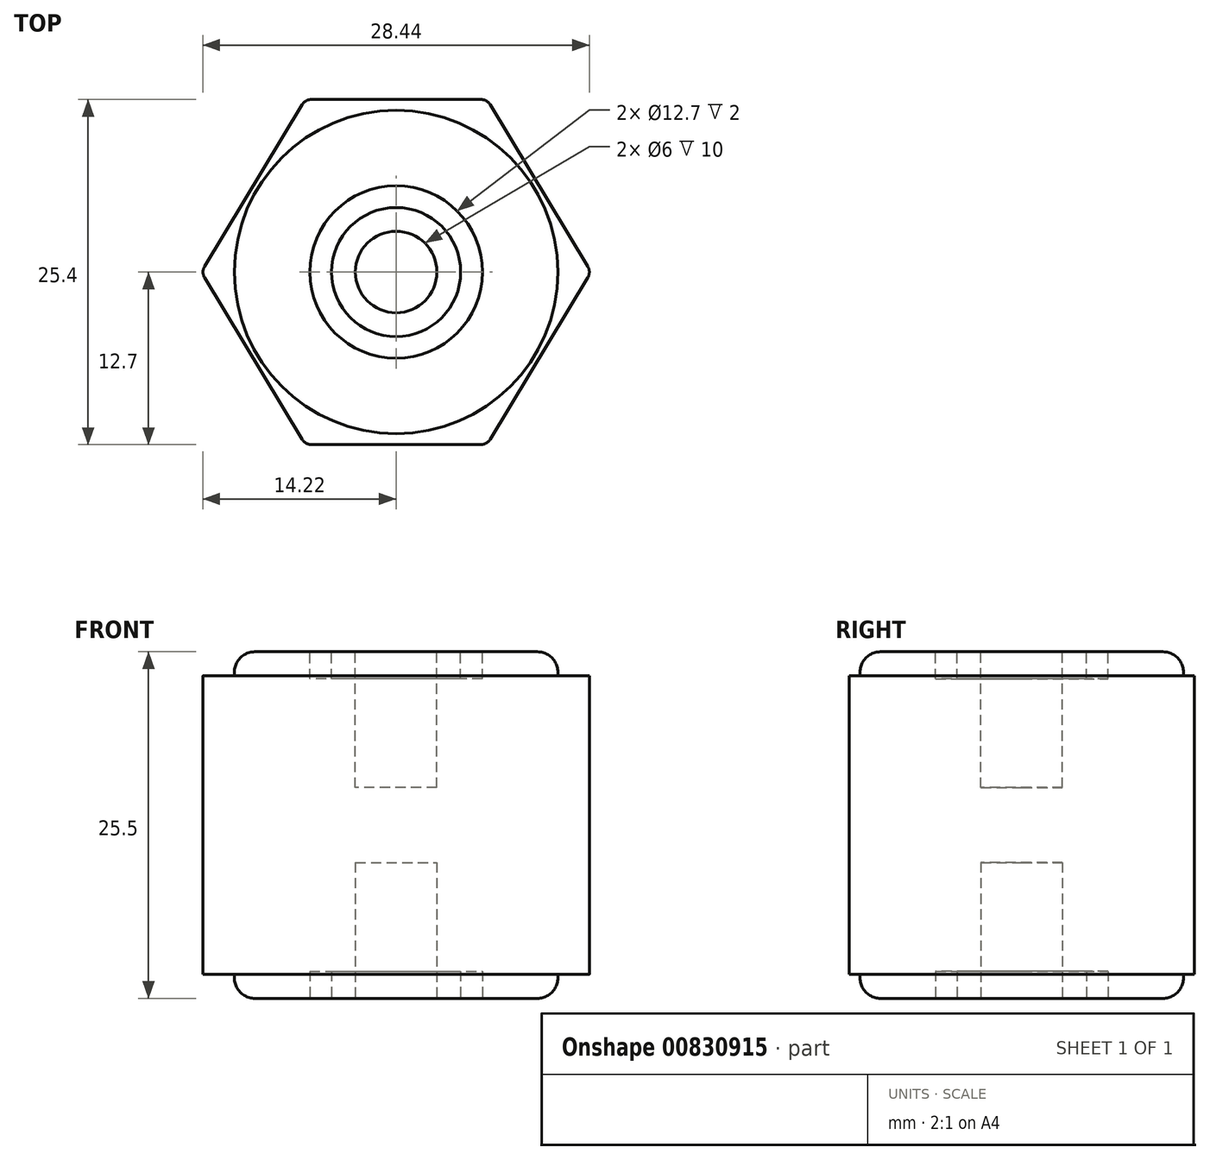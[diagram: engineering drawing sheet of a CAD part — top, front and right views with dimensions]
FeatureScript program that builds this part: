
annotation { "Feature Type Name" : "Feature", "Feature Type Description" : "" }
export const myFeature = defineFeature(function(context is Context, id is Id, definition is map)
    precondition{}
    {
        {
            var Q0;
            Q0=qCreatedBy(makeId("Top.planeOp"),FACE);
            var sketch = newSketch(context, id + "F0", { "sketchPlane" : qUnion([Q0])});
            skCircle(sketch, "E0", {"center": v(0, 0) * mm, "radius": 14.35 * mm});
            skLineSegment(sketch, "E1", {"start": v(-16.5, 12.7) * mm, "end": v(14.66, 12.7) * mm});
            skLineSegment(sketch, "E2", {"start": v(-20.14, -12.7) * mm, "end": v(19.5, -12.7) * mm});
            skLineSegment(sketch, "E3", {"start": v(6.68, 12.7) * mm, "end": v(14.35, 0) * mm});
            skLineSegment(sketch, "E4", {"start": v(14.35, 0) * mm, "end": v(6.68, -12.7) * mm});
            skLineSegment(sketch, "E5", {"start": v(-6.68, 12.7) * mm, "end": v(-14.35, 0) * mm});
            skLineSegment(sketch, "E6", {"start": v(-14.35, 0) * mm, "end": v(-6.68, -12.7) * mm});
            skSolve(sketch);
        }
        {
            var Q0;
            {var subQ1=sQuery(id+"F0.wireOp",EDGE,"E3");Q0=makeQuery(id+"F0.imprint","IMPRINT",FACE,{"disambiguationData":[TD([[makeQuery(id+"F0.imprint","IMPRINT",EDGE,{"derivedFrom":subQ1}),-1.0]])]});}
            extrude(context, id + "F1", {"entities" : qUnion([Q0]), "depth" : 22 * mm, "offsetDistance" : 25 * mm});
        }
        {
            var Q0;
            Q0=makeQuery(id+"F1.opExtrude","CAP_FACE",FACE,{"disambiguationData":[OSD([sQuery(id+"F0.wireOp",EDGE,"E1"),sQuery(id+"F0.wireOp",EDGE,"E2"),sQuery(id+"F0.wireOp",EDGE,"E3"),sQuery(id+"F0.wireOp",EDGE,"E4"),sQuery(id+"F0.wireOp",EDGE,"E5"),sQuery(id+"F0.wireOp",EDGE,"E6")])],"isStart":false});
            var sketch = newSketch(context, id + "F2", { "sketchPlane" : qUnion([Q0])});
            skCircle(sketch, "E7", {"center": v(0, 0) * mm, "radius": 11.9 * mm});
            skSolve(sketch);
        }
        {
            var Q0;
            Q0 = qSketchRegion(id + "F2", true);
            extrude(context, id + "F3", {"entities" : qUnion([Q0]), "operationType" : NewBodyOperationType.ADD, "depth" : 1.75 * mm, "offsetDistance" : 25 * mm});
        }
        {
            var Q0;
            Q0=makeQuery(id+"F1.opExtrude","CAP_FACE",FACE,{"disambiguationData":[OSD([sQuery(id+"F0.wireOp",EDGE,"E1"),sQuery(id+"F0.wireOp",EDGE,"E2"),sQuery(id+"F0.wireOp",EDGE,"E3"),sQuery(id+"F0.wireOp",EDGE,"E4"),sQuery(id+"F0.wireOp",EDGE,"E5"),sQuery(id+"F0.wireOp",EDGE,"E6")])],"isStart":true});
            var sketch = newSketch(context, id + "F4", { "sketchPlane" : qUnion([Q0])});
            skCircle(sketch, "E8", {"center": v(0, 0) * mm, "radius": 11.9 * mm});
            skSolve(sketch);
        }
        {
            var Q0;
            Q0 = qSketchRegion(id + "F4", true);
            extrude(context, id + "F5", {"entities" : qUnion([Q0]), "operationType" : NewBodyOperationType.ADD, "depth" : 1.75 * mm, "offsetDistance" : 25 * mm});
        }
        {
            var Q0;
            Q0=makeQuery(id+"F5.opExtrude","CAP_FACE",FACE,{"disambiguationData":[OSD([sQuery(id+"F4.wireOp",EDGE,"E8")])],"isStart":false});
            var sketch = newSketch(context, id + "F6", { "sketchPlane" : qUnion([Q0])});
            skCircle(sketch, "E9", {"center": v(0, 0) * mm, "radius": 3 * mm});
            skCircle(sketch, "E10", {"center": v(0, 0) * mm, "radius": 6.35 * mm});
            skCircle(sketch, "E11", {"center": v(0, 0) * mm, "radius": 4.75 * mm});
            skSolve(sketch);
        }
        {
            var Q0;
            Q0=makeQuery(id+"F3.opExtrude","CAP_FACE",FACE,{"disambiguationData":[OSD([sQuery(id+"F2.wireOp",EDGE,"E7")])],"isStart":false});
            var sketch = newSketch(context, id + "F7", { "sketchPlane" : qUnion([Q0])});
            skCircle(sketch, "E12", {"center": v(0, 0) * mm, "radius": 3 * mm});
            skCircle(sketch, "E13", {"center": v(0, 0) * mm, "radius": 6.35 * mm});
            skCircle(sketch, "E14", {"center": v(0, 0) * mm, "radius": 4.75 * mm});
            skSolve(sketch);
        }
        {
            var Q0;
            Q0 = qSketchRegion(id + "F6", true);
            extrude(context, id + "F8", {"entities" : qUnion([Q0]), "operationType" : NewBodyOperationType.REMOVE, "oppositeDirection" : true, "depth" : 2 * mm, "offsetDistance" : 25 * mm});
        }
        {
            var Q0;
            Q0=makeQuery(id+"F7.imprint","IMPRINT",FACE,{"disambiguationData":[TD([[makeQuery(id+"F7.imprint","IMPRINT",EDGE,{"derivedFrom":sQuery(id+"F7.wireOp",EDGE,"E13")}),1.0]])]});
            extrude(context, id + "F9", {"entities" : qUnion([Q0]), "operationType" : NewBodyOperationType.REMOVE, "oppositeDirection" : true, "depth" : 2 * mm, "offsetDistance" : 25 * mm});
        }
        {
            var Q0;
            Q0=makeQuery(id+"F7.imprint","IMPRINT",FACE,{"disambiguationData":[TD([[makeQuery(id+"F7.imprint","IMPRINT",EDGE,{"derivedFrom":sQuery(id+"F7.wireOp",EDGE,"E12")}),1.0]])]});
            extrude(context, id + "F10", {"entities" : qUnion([Q0]), "operationType" : NewBodyOperationType.REMOVE, "oppositeDirection" : true, "depth" : 10 * mm, "offsetDistance" : 25 * mm});
        }
        {
            var Q0;
            Q0=makeQuery(id+"F6.imprint","IMPRINT",FACE,{"disambiguationData":[TD([[makeQuery(id+"F6.imprint","IMPRINT",EDGE,{"derivedFrom":sQuery(id+"F6.wireOp",EDGE,"E9")}),1.0]])]});
            extrude(context, id + "F11", {"entities" : qUnion([Q0]), "operationType" : NewBodyOperationType.REMOVE, "oppositeDirection" : true, "depth" : 10 * mm, "offsetDistance" : 25 * mm});
        }
        {
            var Q0;
            Q0=makeQuery(id+"F3.opExtrude","CAP_EDGE",EDGE,{"disambiguationData":[OSD([sQuery(id+"F2.wireOp",EDGE,"E7")])],"isStart":false});
            var Q1;
            Q1=makeQuery(id+"F5.opExtrude","CAP_EDGE",EDGE,{"disambiguationData":[OSD([sQuery(id+"F4.wireOp",EDGE,"E8")])],"isStart":false});
            fillet(context, id + "F12", {"entities" : qUnion([Q0, Q1]), "radius" : 1.5 * mm, "tangentPropagation" : true, "allowEdgeOverflow" : false});
        }
        {
            var Q0;
            Q0=makeQuery(id+"F1.opExtrude","SWEPT_EDGE",EDGE,{"disambiguationData":[OSD([sQuery(id+"F0.wireOp",EDGE,"E0"),sQuery(id+"F0.wireOp",EDGE,"E1"),sQuery(id+"F0.wireOp",EDGE,"E5")])]});
            var Q1;
            Q1=makeQuery(id+"F1.opExtrude","SWEPT_EDGE",EDGE,{"disambiguationData":[OSD([sQuery(id+"F0.wireOp",EDGE,"E0"),sQuery(id+"F0.wireOp",EDGE,"E1"),sQuery(id+"F0.wireOp",EDGE,"E3")])]});
            var Q2;
            Q2=makeQuery(id+"F1.opExtrude","SWEPT_EDGE",EDGE,{"disambiguationData":[OSD([sQuery(id+"F0.wireOp",EDGE,"E0"),sQuery(id+"F0.wireOp",EDGE,"E3"),sQuery(id+"F0.wireOp",EDGE,"E4")])]});
            var Q3;
            Q3=makeQuery(id+"F1.opExtrude","SWEPT_EDGE",EDGE,{"disambiguationData":[OSD([sQuery(id+"F0.wireOp",EDGE,"E0"),sQuery(id+"F0.wireOp",EDGE,"E2"),sQuery(id+"F0.wireOp",EDGE,"E4")])]});
            var Q4;
            Q4=makeQuery(id+"F1.opExtrude","SWEPT_EDGE",EDGE,{"disambiguationData":[OSD([sQuery(id+"F0.wireOp",EDGE,"E0"),sQuery(id+"F0.wireOp",EDGE,"E2"),sQuery(id+"F0.wireOp",EDGE,"E6")])]});
            var Q5;
            Q5=makeQuery(id+"F1.opExtrude","SWEPT_EDGE",EDGE,{"disambiguationData":[OSD([sQuery(id+"F0.wireOp",EDGE,"E0"),sQuery(id+"F0.wireOp",EDGE,"E5"),sQuery(id+"F0.wireOp",EDGE,"E6")])]});
            fillet(context, id + "F13", {"entities" : qUnion([Q0, Q1, Q2, Q3, Q4, Q5]), "radius" : .8 * mm, "tangentPropagation" : true, "allowEdgeOverflow" : false});
        }
    });
